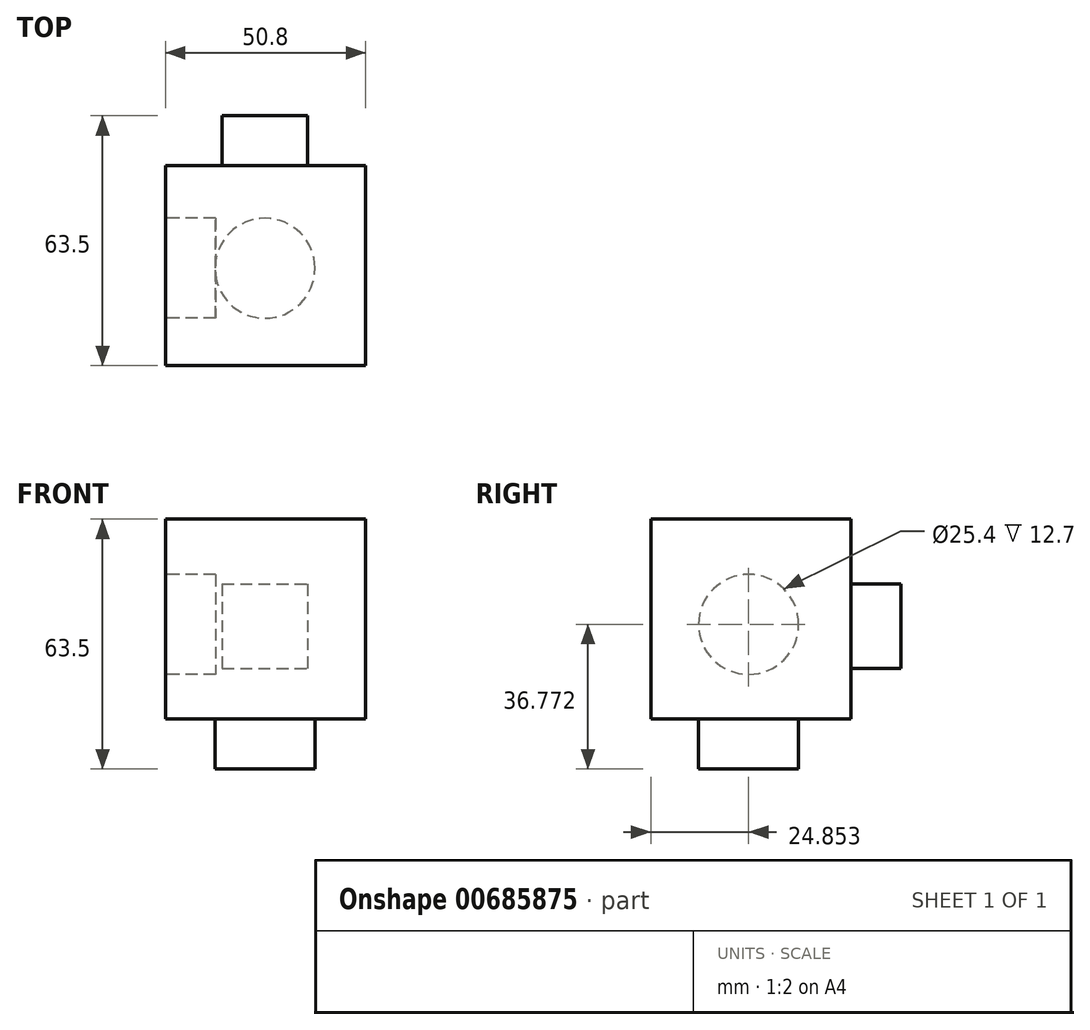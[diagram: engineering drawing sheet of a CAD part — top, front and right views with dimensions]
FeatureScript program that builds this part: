
annotation { "Feature Type Name" : "Feature", "Feature Type Description" : "" }
export const myFeature = defineFeature(function(context is Context, id is Id, definition is map)
    precondition{}
    {
        {
            var Q0;
            Q0=qCreatedBy(makeId("Front.planeOp"),FACE);
            var sketch = newSketch(context, id + "F0", { "sketchPlane" : qUnion([Q0])});
            skLineSegment(sketch, "E0.bottom", {"start": v(0, 0) * mm, "end": v(-50.8, 0) * mm});
            skLineSegment(sketch, "E0.top", {"start": v(0, 50.8) * mm, "end": v(-50.8, 50.8) * mm});
            skLineSegment(sketch, "E0.left", {"start": v(0, 0) * mm, "end": v(0, 50.8) * mm});
            skLineSegment(sketch, "E0.right", {"start": v(-50.8, 0) * mm, "end": v(-50.8, 50.8) * mm});
            skSolve(sketch);
        }
        {
            var Q0;
            Q0 = qSketchRegion(id + "F0", true);
            extrude(context, id + "F1", {"entities" : qUnion([Q0]), "depth" : 50.8 * mm, "offsetDistance" : 25.4 * mm});
        }
        {
            var Q0;
            Q0=qCreatedBy(makeId("Front.planeOp"),FACE);
            var sketch = newSketch(context, id + "F2", { "sketchPlane" : qUnion([Q0])});
            skLineSegment(sketch, "E1.bottom", {"start": v(-36.4, 34.33) * mm, "end": v(-14.7, 34.33) * mm});
            skLineSegment(sketch, "E1.top", {"start": v(-36.4, 12.83) * mm, "end": v(-14.7, 12.83) * mm});
            skLineSegment(sketch, "E1.left", {"start": v(-36.4, 34.33) * mm, "end": v(-36.4, 12.83) * mm});
            skLineSegment(sketch, "E1.right", {"start": v(-14.7, 34.33) * mm, "end": v(-14.7, 12.83) * mm});
            skSolve(sketch);
        }
        {
            var Q0;
            Q0=makeQuery(id+"F2.imprint","IMPRINT",FACE,{"disambiguationData":[TD([[makeQuery(id+"F2.imprint","IMPRINT",EDGE,{"derivedFrom":sQuery(id+"F2.wireOp",EDGE,"E1.bottom")}),-1.0]])]});
            extrude(context, id + "F3", {"entities" : qUnion([Q0]), "operationType" : NewBodyOperationType.ADD, "oppositeDirection" : true, "depth" : 12.7 * mm, "offsetDistance" : 25.4 * mm});
        }
        {
            var Q0;
            Q0=makeQuery(id+"F1.opExtrude","SWEPT_FACE",FACE,{"disambiguationData":[OSD([sQuery(id+"F0.wireOp",EDGE,"E0.right")])]});
            var sketch = newSketch(context, id + "F4", { "sketchPlane" : qUnion([Q0])});
            skCircle(sketch, "E2", {"center": v(25.95, 24.07) * mm, "radius": 12.7 * mm});
            skSolve(sketch);
        }
        {
            var Q0;
            Q0 = qSketchRegion(id + "F4", true);
            extrude(context, id + "F5", {"entities" : qUnion([Q0]), "operationType" : NewBodyOperationType.REMOVE, "oppositeDirection" : true, "depth" : 12.7 * mm, "offsetDistance" : 25.4 * mm});
        }
        {
            var Q0;
            Q0=makeQuery(id+"F1.opExtrude","SWEPT_FACE",FACE,{"disambiguationData":[OSD([sQuery(id+"F0.wireOp",EDGE,"E0.bottom")])]});
            var sketch = newSketch(context, id + "F6", { "sketchPlane" : qUnion([Q0])});
            skCircle(sketch, "E3", {"center": v(-25.55, 26.04) * mm, "radius": 12.7 * mm});
            skSolve(sketch);
        }
        {
            var Q0;
            Q0 = qSketchRegion(id + "F6", true);
            extrude(context, id + "F7", {"entities" : qUnion([Q0]), "operationType" : NewBodyOperationType.ADD, "depth" : 12.7 * mm, "offsetDistance" : 25.4 * mm});
        }
    });
